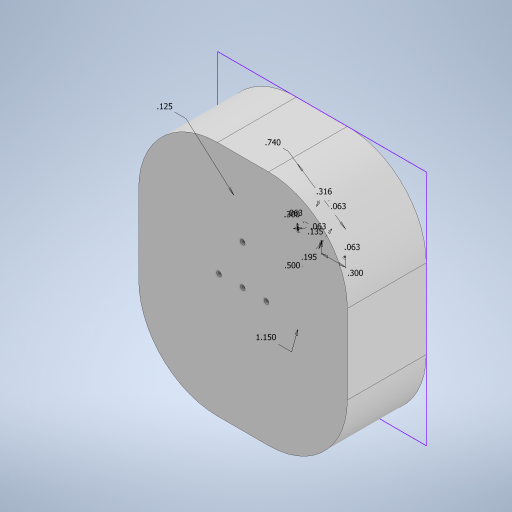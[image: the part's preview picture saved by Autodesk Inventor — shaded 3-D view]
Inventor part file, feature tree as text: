
AUTODESK INVENTOR PART (.ipt)
format: ipt  version: 2023 (Build 270158000, 158)  size: 518,144 bytes
history: native  units: in
note: dims shown in document units (in); Inventor stores cm internally (conversion verified against a paired STEP export)
features: extrude x3, fillet x2, sketch x1
ambient origin geometry x8: Origin, YZ Plane, XZ Plane, XY Plane, X Axis, Y Axis, Z Axis, Center Point
bodies: Body1 (feature_tree)
feature tree (6):
  sketch  "Sketch1"  dims[d3=0.866in d15=0.75in d20=0.316in d37=0.75in d44=0.125in d57=0.74in d70=0.135in d73=1.15in d76=0.3in d77=0.3in d84=0.5in d85=0.195in d97=0.0625in d98=0.0625in d99=0.0625in d100=0.0625in d101=1.0in d102=0.0in d103=0.76in d104=0.0in d105=0.45in d106=0.0in d107=0.04in d108=1.0in]
  extrude  "Extrusion22"  Depth=1.0in
  extrude  "Extrusion23"  Depth=1.0in
  extrude  "Extrusion24"  Depth=1.0in
  fillet  "Fillet4"  Radius=0.74in
  fillet  "Fillet5"  Radius=0.135in
